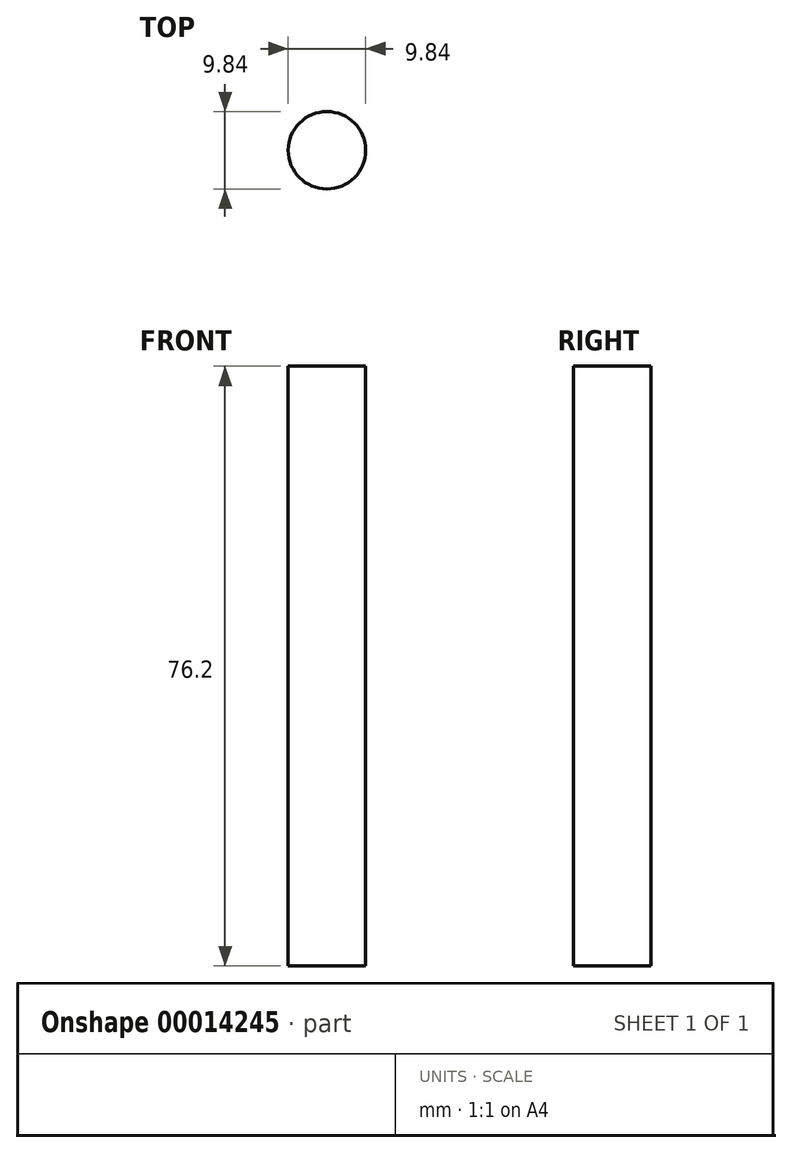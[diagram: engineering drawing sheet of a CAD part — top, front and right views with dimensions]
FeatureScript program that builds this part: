
annotation { "Feature Type Name" : "Feature", "Feature Type Description" : "" }
export const myFeature = defineFeature(function(context is Context, id is Id, definition is map)
    precondition{}
    {
        {
            var Q0;
            Q0=qCreatedBy(makeId("Top.planeOp"),FACE);
            var sketch = newSketch(context, id + "F0", { "sketchPlane" : qUnion([Q0])});
            skCircle(sketch, "E0", {"center": v(0, 0) * mm, "radius": 4.92 * mm});
            skSolve(sketch);
        }
        {
            var Q0;
            Q0=sQuery(id+"F0.wireOp",EDGE,"E0");
            extrude(context, id + "F1", {"bodyType" : ToolBodyType.SURFACE, "surfaceEntities" : qUnion([Q0]), "depth" : 76.2 * mm});
        }
    });
